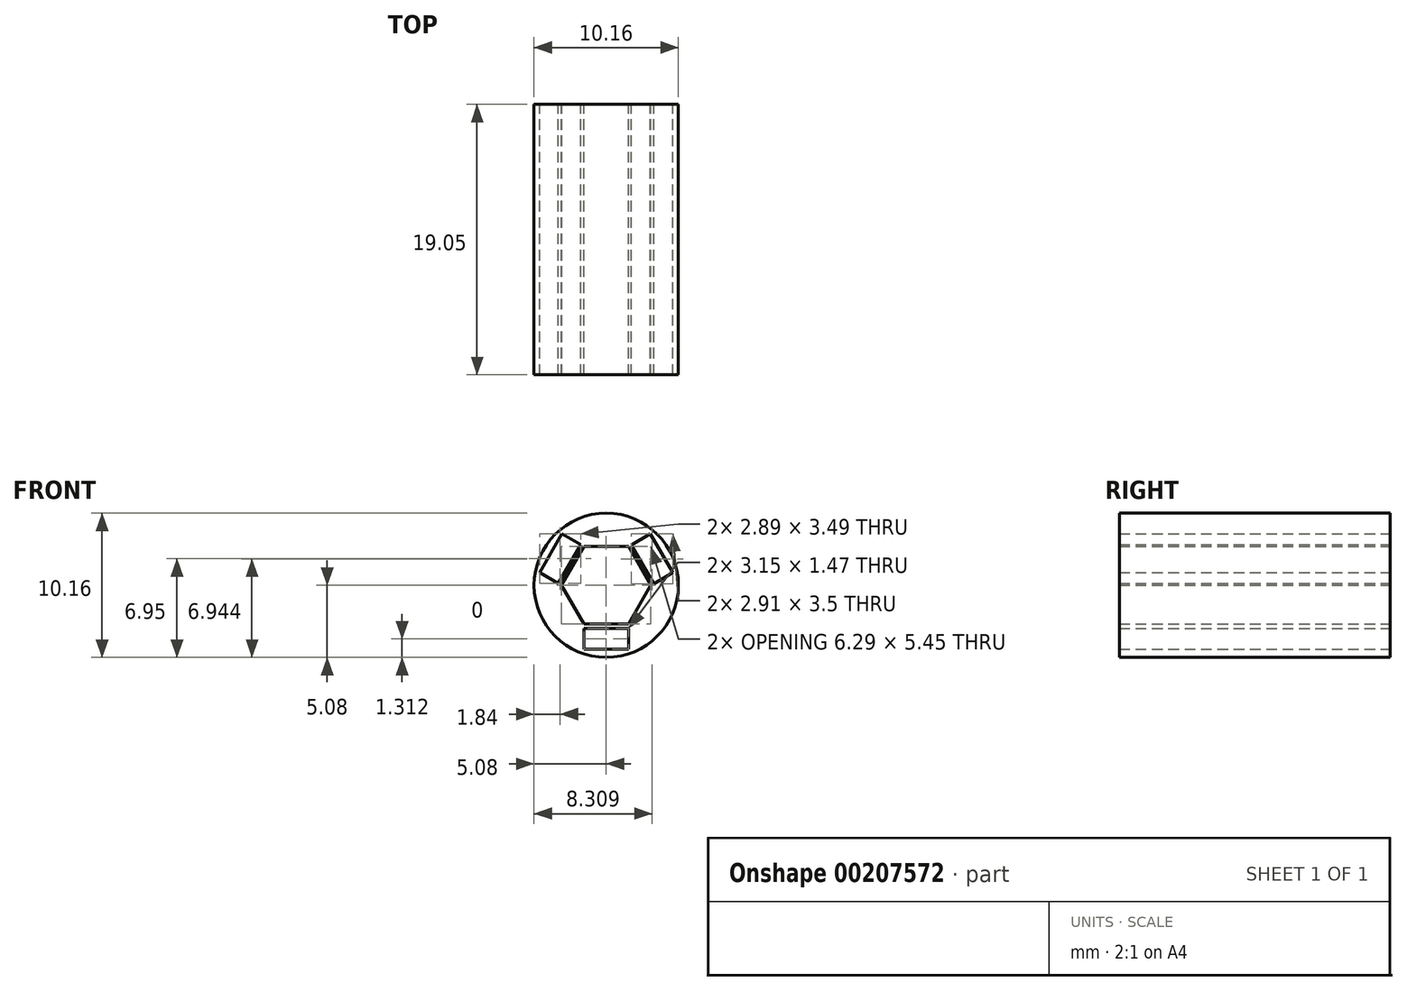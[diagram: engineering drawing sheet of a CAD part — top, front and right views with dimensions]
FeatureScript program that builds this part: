
annotation { "Feature Type Name" : "Feature", "Feature Type Description" : "" }
export const myFeature = defineFeature(function(context is Context, id is Id, definition is map)
    precondition{}
    {
        {
            var Q0;
            Q0=qCreatedBy(makeId("Front.planeOp"),FACE);
            var sketch = newSketch(context, id + "F0", { "sketchPlane" : qUnion([Q0])});
            skCircle(sketch, "E0.cCircle", {"center": v(0, 0) * mm, "radius": 2.73 * mm, "construction": true});
            skLineSegment(sketch, "E0.0", {"start": v(3.15, 0) * mm, "end": v(1.57, -2.73) * mm});
            skLineSegment(sketch, "E0.1", {"start": v(1.57, -2.73) * mm, "end": v(-1.57, -2.73) * mm});
            skLineSegment(sketch, "E0.2", {"start": v(-1.57, -2.72) * mm, "end": v(-3.15, 0) * mm});
            skLineSegment(sketch, "E0.3", {"start": v(-3.15, 0) * mm, "end": v(-1.57, 2.73) * mm});
            skLineSegment(sketch, "E0.4", {"start": v(-1.57, 2.73) * mm, "end": v(1.57, 2.73) * mm});
            skLineSegment(sketch, "E0.5", {"start": v(1.57, 2.73) * mm, "end": v(3.15, 0) * mm});
            skPoint(sketch, "E0.0.midPoint", {"position": v(2.36, -1.36) * mm});
            skLineSegment(sketch, "E1", {"start": v(0, 2.73) * mm, "end": v(0, -2.73) * mm, "construction": true});
            skCircle(sketch, "E2", {"center": v(0, 0) * mm, "radius": 5.08 * mm});
            skLineSegment(sketch, "E3", {"start": v(1.77, 2.84) * mm, "end": v(3.11, 3.61) * mm});
            skLineSegment(sketch, "E4", {"start": v(3.11, 3.61) * mm, "end": v(4.69, 0.89) * mm});
            skLineSegment(sketch, "E5", {"start": v(4.69, 0.89) * mm, "end": v(3.35, 0.11) * mm});
            skLineSegment(sketch, "E6", {"start": v(-1.8, 2.85) * mm, "end": v(-3.11, 3.61) * mm});
            skLineSegment(sketch, "E7", {"start": v(-3.11, 3.61) * mm, "end": v(-4.69, 0.89) * mm});
            skLineSegment(sketch, "E8", {"start": v(-4.69, 0.89) * mm, "end": v(-3.37, 0.13) * mm});
            skLineSegment(sketch, "E9", {"start": v(-1.57, -3.03) * mm, "end": v(-1.57, -4.5) * mm});
            skLineSegment(sketch, "E10", {"start": v(-1.57, -4.5) * mm, "end": v(1.57, -4.5) * mm});
            skLineSegment(sketch, "E11", {"start": v(1.57, -4.5) * mm, "end": v(1.57, -3.03) * mm});
            skLineSegment(sketch, "E12", {"start": v(1.77, 2.84) * mm, "end": v(3.35, 0.11) * mm});
            skLineSegment(sketch, "E13", {"start": v(-1.8, 2.85) * mm, "end": v(-3.37, 0.13) * mm});
            skLineSegment(sketch, "E14", {"start": v(1.57, -3.03) * mm, "end": v(-1.57, -3.03) * mm});
            skSolve(sketch);
        }
        {
            var Q0;
            Q0=makeQuery(id+"F0.imprint","IMPRINT",FACE,{"disambiguationData":[TD([[makeQuery(id+"F0.imprint","IMPRINT",EDGE,{"derivedFrom":sQuery(id+"F0.wireOp",EDGE,"E0.0")}),1.0]])]});
            extrude(context, id + "F1", {"entities" : qUnion([Q0]), "depth" : 19.05 * mm});
        }
        {
            var Q0;
            Q0=makeQuery(id+"F1.opExtrude","SWEPT_BODY",BODY,{"disambiguationData":[OSD([sQuery(id+"F0.wireOp",EDGE,"E0.0"),sQuery(id+"F0.wireOp",EDGE,"E0.1"),sQuery(id+"F0.wireOp",EDGE,"E0.2"),sQuery(id+"F0.wireOp",EDGE,"E0.3"),sQuery(id+"F0.wireOp",EDGE,"E0.4"),sQuery(id+"F0.wireOp",EDGE,"E0.5"),sQuery(id+"F0.wireOp",EDGE,"E2")])]});
            transform(context, id + "F2", {"entities" : qUnion([Q0]), "transformType" : TransformType.TRANSLATION_3D, "dx" : 0 * mm, "dy" : 0 * mm, "dz" : 0 * mm, "makeCopy" : true});
        }
    });
